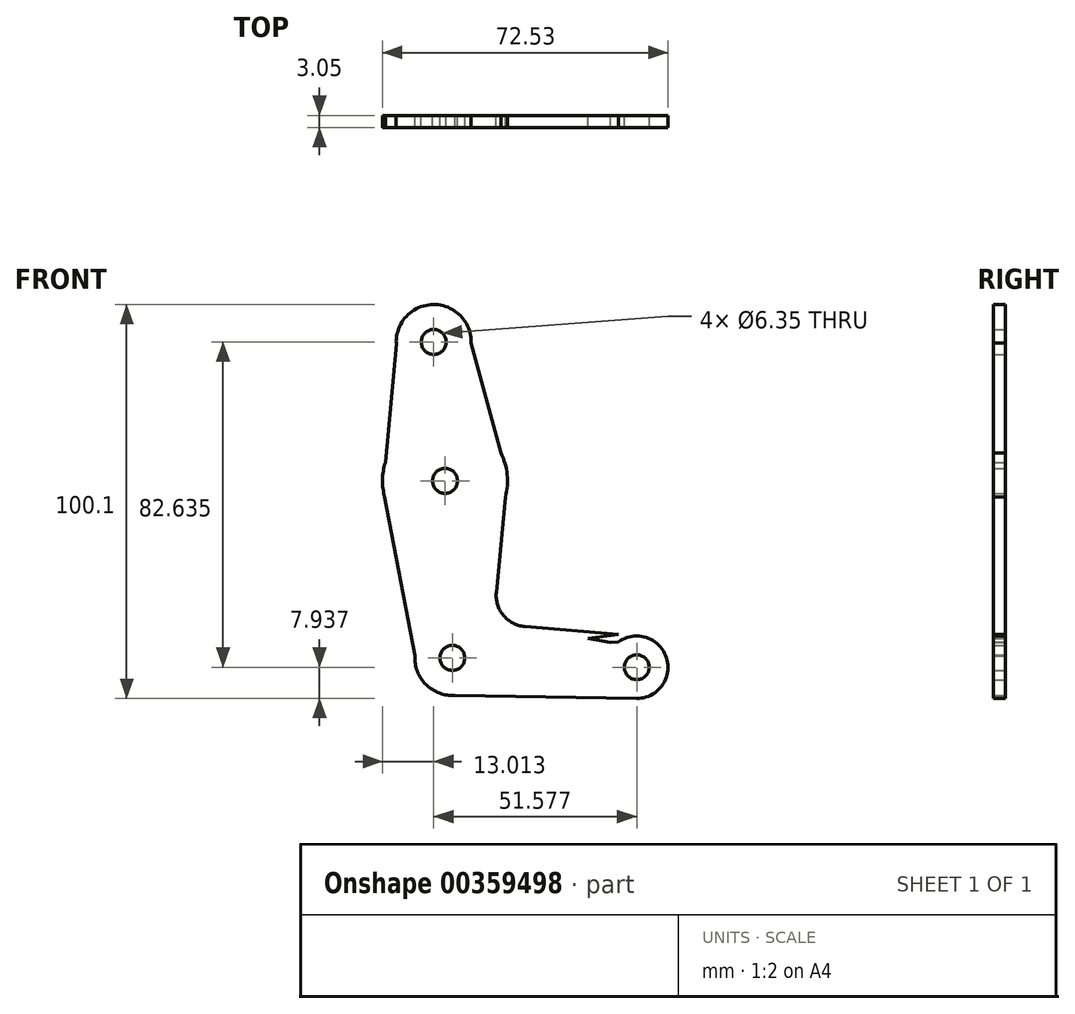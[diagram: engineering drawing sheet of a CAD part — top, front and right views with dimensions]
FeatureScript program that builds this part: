
annotation { "Feature Type Name" : "Feature", "Feature Type Description" : "" }
export const myFeature = defineFeature(function(context is Context, id is Id, definition is map)
    precondition{}
    {
        {
            var Q0;
            Q0=qCreatedBy(makeId("Front.planeOp"),FACE);
            var sketch = newSketch(context, id + "F0", { "sketchPlane" : qUnion([Q0])});
            skCircle(sketch, "E0", {"center": v(-51.58, 52.66) * mm, "radius": 9.53 * mm});
            skCircle(sketch, "E1", {"center": v(-48.72, 17.38) * mm, "radius": 15.88 * mm});
            skCircle(sketch, "E2", {"center": v(-46.86, -27.61) * mm, "radius": 9.53 * mm});
            skCircle(sketch, "E3", {"center": v(0, -29.97) * mm, "radius": 7.94 * mm});
            skLineSegment(sketch, "E4", {"start": v(-61.1, 52.2) * mm, "end": v(-64.49, 15.57) * mm});
            skLineSegment(sketch, "E5", {"start": v(-42.05, 52.43) * mm, "end": v(-32.88, 18.44) * mm});
            skLineSegment(sketch, "E6", {"start": v(-64.49, 15.57) * mm, "end": v(-56.37, -27.07) * mm});
            skLineSegment(sketch, "E7", {"start": v(-46.14, -37.1) * mm, "end": v(0, -37.91) * mm});
            skCircle(sketch, "E8", {"center": v(-51.58, 52.66) * mm, "radius": 3.18 * mm});
            skCircle(sketch, "E9", {"center": v(-48.72, 17.38) * mm, "radius": 3.18 * mm});
            skCircle(sketch, "E10", {"center": v(-46.86, -27.61) * mm, "radius": 3.18 * mm});
            skCircle(sketch, "E11", {"center": v(0, -29.97) * mm, "radius": 3.18 * mm});
            skLineSegment(sketch, "E12", {"start": v(-32.88, 18.44) * mm, "end": v(-35.7, -10.95) * mm});
            skLineSegment(sketch, "E13", {"start": v(-28.44, -19.63) * mm, "end": v(0, -22) * mm});
            skPoint(sketch, "E14.newPointB", {"position": v(-46.86, -18.09) * mm});
            skArc(sketch, "E14.filletArc", {"start": v(-35.7, -10.95) * mm, "mid": v(-33.88, -16.8) * mm, "end": v(-28.44, -19.63) * mm});
            skLineSegment(sketch, "E15", {"start": v(-32.88, 18.44) * mm, "end": v(-37.47, -26.01) * mm});
            skPoint(sketch, "E15.endSnap0", {"position": v(-37.47, 35.44) * mm});
            skLineSegment(sketch, "E16", {"start": v(-46.86, -18.09) * mm, "end": v(0, -22) * mm});
            skLineSegment(sketch, "E17", {"start": v(-37.47, -26.01) * mm, "end": v(-28.44, -19.63) * mm});
            skLineSegment(sketch, "E18", {"start": v(-37.47, -26.01) * mm, "end": v(-7.89, -29.07) * mm});
            skLineSegment(sketch, "E19", {"start": v(-37.47, -26.01) * mm, "end": v(-4.7, -23.57) * mm});
            skLineSegment(sketch, "E20", {"start": v(-37.47, -26.01) * mm, "end": v(-16.77, -20.6) * mm});
            skLineSegment(sketch, "E21", {"start": v(-37.47, -26.01) * mm, "end": v(-4.7, -21.62) * mm});
            skLineSegment(sketch, "E22", {"start": v(-37.47, -26.01) * mm, "end": v(-6.62, -23.71) * mm});
            skLineSegment(sketch, "E23", {"start": v(-4.7, -21.62) * mm, "end": v(-4.7, -23.57) * mm});
            skLineSegment(sketch, "E24", {"start": v(-12.43, -22.65) * mm, "end": v(-6.62, -23.71) * mm});
            skSolve(sketch);
        }
        {
            var Q0;
            {var subQ0=sQuery(id+"F0.wireOp",EDGE,"E5");var subQ1=sQuery(id+"F0.wireOp",EDGE,"E1");var subQ3=makeQuery(id+"F0.imprint","INTERSECT",VERTEX,{"derivedFrom":[subQ1,subQ0]});Q0=makeQuery(id+"F0.imprint","IMPRINT",FACE,{"disambiguationData":[TD([[makeQuery(id+"F0.imprint","IMPRINT",EDGE,{"disambiguationData":[TD([[subQ3,1.0]])],"derivedFrom":subQ1}),1.0]])]});}
            var Q1;
            {var subQ0=sQuery(id+"F0.wireOp",EDGE,"E4");var subQ1=sQuery(id+"F0.wireOp",EDGE,"E1");var subQ3=makeQuery(id+"F0.imprint","INTERSECT",VERTEX,{"derivedFrom":[subQ1,subQ0]});Q1=makeQuery(id+"F0.imprint","IMPRINT",FACE,{"disambiguationData":[TD([[makeQuery(id+"F0.imprint","IMPRINT",EDGE,{"disambiguationData":[TD([[subQ3,-1.0]])],"derivedFrom":subQ1}),1.0]])]});}
            var Q2;
            {var subQ0=sQuery(id+"F0.wireOp",EDGE,"E6");var subQ1=sQuery(id+"F0.wireOp",EDGE,"E1");var subQ3=makeQuery(id+"F0.imprint","INTERSECT",VERTEX,{"derivedFrom":[subQ1,subQ0]});Q2=makeQuery(id+"F0.imprint","IMPRINT",FACE,{"disambiguationData":[TD([[makeQuery(id+"F0.imprint","IMPRINT",EDGE,{"disambiguationData":[TD([[subQ3,1.0]])],"derivedFrom":subQ1}),1.0]])]});}
            var Q3;
            {var subQ0=sQuery(id+"F0.wireOp",EDGE,"E12");var subQ1=sQuery(id+"F0.wireOp",EDGE,"E1");var subQ3=makeQuery(id+"F0.imprint","INTERSECT",VERTEX,{"derivedFrom":[subQ1,subQ0]});Q3=makeQuery(id+"F0.imprint","IMPRINT",FACE,{"disambiguationData":[TD([[makeQuery(id+"F0.imprint","IMPRINT",EDGE,{"disambiguationData":[TD([[subQ3,-1.0]])],"derivedFrom":subQ1}),1.0]])]});}
            var Q4;
            Q4=makeQuery(id+"F0.imprint","IMPRINT",FACE,{"disambiguationData":[TD([[makeQuery(id+"F0.imprint","IMPRINT",EDGE,{"derivedFrom":sQuery(id+"F0.wireOp",EDGE,"E8")}),-1.0]])]});
            var Q5;
            {var subQ0=sQuery(id+"F0.wireOp",EDGE,"E4");var subQ1=sQuery(id+"F0.wireOp",EDGE,"E0");var subQ2=makeQuery(id+"F0.imprint","INTERSECT",VERTEX,{"derivedFrom":[subQ1,subQ0]});Q5=makeQuery(id+"F0.imprint","IMPRINT",FACE,{"disambiguationData":[TD([[makeQuery(id+"F0.imprint","IMPRINT",EDGE,{"disambiguationData":[TD([[subQ2,-1.0]])],"derivedFrom":subQ1}),-1.0]])]});}
            var Q6;
            {var subQ0=sQuery(id+"F0.wireOp",EDGE,"E17");Q6=makeQuery(id+"F0.imprint","IMPRINT",FACE,{"disambiguationData":[TD([[makeQuery(id+"F0.imprint","IMPRINT",EDGE,{"derivedFrom":subQ0}),-1.0]])]});}
            var Q7;
            {var subQ1=sQuery(id+"F0.wireOp",EDGE,"E2");var subQ3=sQuery(id+"F0.wireOp",EDGE,"E16");var subQ4=makeQuery(id+"F0.imprint","INTERSECT",VERTEX,{"derivedFrom":[subQ1,subQ3]});Q7=makeQuery(id+"F0.imprint","IMPRINT",FACE,{"disambiguationData":[TD([[makeQuery(id+"F0.imprint","IMPRINT",EDGE,{"disambiguationData":[TD([[subQ4,-1.0]])],"derivedFrom":subQ3}),-1.0]])]});}
            var Q8;
            {var subQ0=sQuery(id+"F0.wireOp",EDGE,"E20");Q8=makeQuery(id+"F0.imprint","IMPRINT",FACE,{"disambiguationData":[TD([[makeQuery(id+"F0.imprint","IMPRINT",EDGE,{"derivedFrom":subQ0}),-1.0]])]});}
            var Q9;
            {var subQ1=sQuery(id+"F0.wireOp",EDGE,"E1");var subQ5=sQuery(id+"F0.wireOp",EDGE,"E6");var subQ9=makeQuery(id+"F0.imprint","INTERSECT",VERTEX,{"derivedFrom":[subQ1,subQ5]});Q9=makeQuery(id+"F0.imprint","IMPRINT",FACE,{"disambiguationData":[TD([[makeQuery(id+"F0.imprint","IMPRINT",EDGE,{"disambiguationData":[TD([[subQ9,-1.0]])],"derivedFrom":subQ1}),-1.0]])]});}
            var Q10;
            {var subQ0=sQuery(id+"F0.wireOp",EDGE,"E18");Q10=makeQuery(id+"F0.imprint","IMPRINT",FACE,{"disambiguationData":[TD([[makeQuery(id+"F0.imprint","IMPRINT",EDGE,{"derivedFrom":subQ0}),-1.0]])]});}
            var Q11;
            Q11=makeQuery(id+"F0.imprint","IMPRINT",FACE,{"disambiguationData":[TD([[makeQuery(id+"F0.imprint","IMPRINT",EDGE,{"derivedFrom":sQuery(id+"F0.wireOp",EDGE,"E10")}),-1.0]])]});
            var Q12;
            {var subQ0=sQuery(id+"F0.wireOp",EDGE,"E17");Q12=makeQuery(id+"F0.imprint","IMPRINT",FACE,{"disambiguationData":[TD([[makeQuery(id+"F0.imprint","IMPRINT",EDGE,{"derivedFrom":subQ0}),1.0]])]});}
            var Q13;
            {var subQ5=sQuery(id+"F0.wireOp",EDGE,"E14.filletArc");Q13=makeQuery(id+"F0.imprint","IMPRINT",FACE,{"disambiguationData":[TD([[makeQuery(id+"F0.imprint","IMPRINT",EDGE,{"derivedFrom":subQ5}),-1.0]])]});}
            var Q14;
            {var subQ0=sQuery(id+"F0.wireOp",EDGE,"E12");var subQ1=sQuery(id+"F0.wireOp",EDGE,"E1");var subQ2=makeQuery(id+"F0.imprint","INTERSECT",VERTEX,{"derivedFrom":[subQ1,subQ0]});Q14=makeQuery(id+"F0.imprint","IMPRINT",FACE,{"disambiguationData":[TD([[makeQuery(id+"F0.imprint","IMPRINT",EDGE,{"disambiguationData":[TD([[subQ2,1.0]])],"derivedFrom":subQ1}),1.0]])]});}
            var Q15;
            Q15=makeQuery(id+"F0.imprint","IMPRINT",FACE,{"disambiguationData":[TD([[makeQuery(id+"F0.imprint","IMPRINT",EDGE,{"derivedFrom":sQuery(id+"F0.wireOp",EDGE,"E9")}),-1.0]])]});
            var Q16;
            {var subQ0=sQuery(id+"F0.wireOp",EDGE,"E18");Q16=makeQuery(id+"F0.imprint","IMPRINT",FACE,{"disambiguationData":[TD([[makeQuery(id+"F0.imprint","IMPRINT",EDGE,{"derivedFrom":subQ0}),1.0]])]});}
            var Q17;
            {var subQ0=sQuery(id+"F0.wireOp",EDGE,"E22");Q17=makeQuery(id+"F0.imprint","IMPRINT",FACE,{"disambiguationData":[TD([[makeQuery(id+"F0.imprint","IMPRINT",EDGE,{"derivedFrom":subQ0}),1.0]])]});}
            var Q18;
            Q18=makeQuery(id+"F0.imprint","IMPRINT",FACE,{"disambiguationData":[TD([[makeQuery(id+"F0.imprint","IMPRINT",EDGE,{"derivedFrom":sQuery(id+"F0.wireOp",EDGE,"E19")}),1.0]])]});
            var Q19;
            Q19=makeQuery(id+"F0.imprint","IMPRINT",FACE,{"disambiguationData":[TD([[makeQuery(id+"F0.imprint","IMPRINT",EDGE,{"derivedFrom":sQuery(id+"F0.wireOp",EDGE,"E11")}),-1.0]])]});
            extrude(context, id + "F1", {"entities" : qUnion([Q0, Q1, Q2, Q3, Q4, Q5, Q6, Q7, Q8, Q9, Q10, Q11, Q12, Q13, Q14, Q15, Q16, Q17, Q18, Q19]), "depth" : 3.05 * mm});
        }
    });
